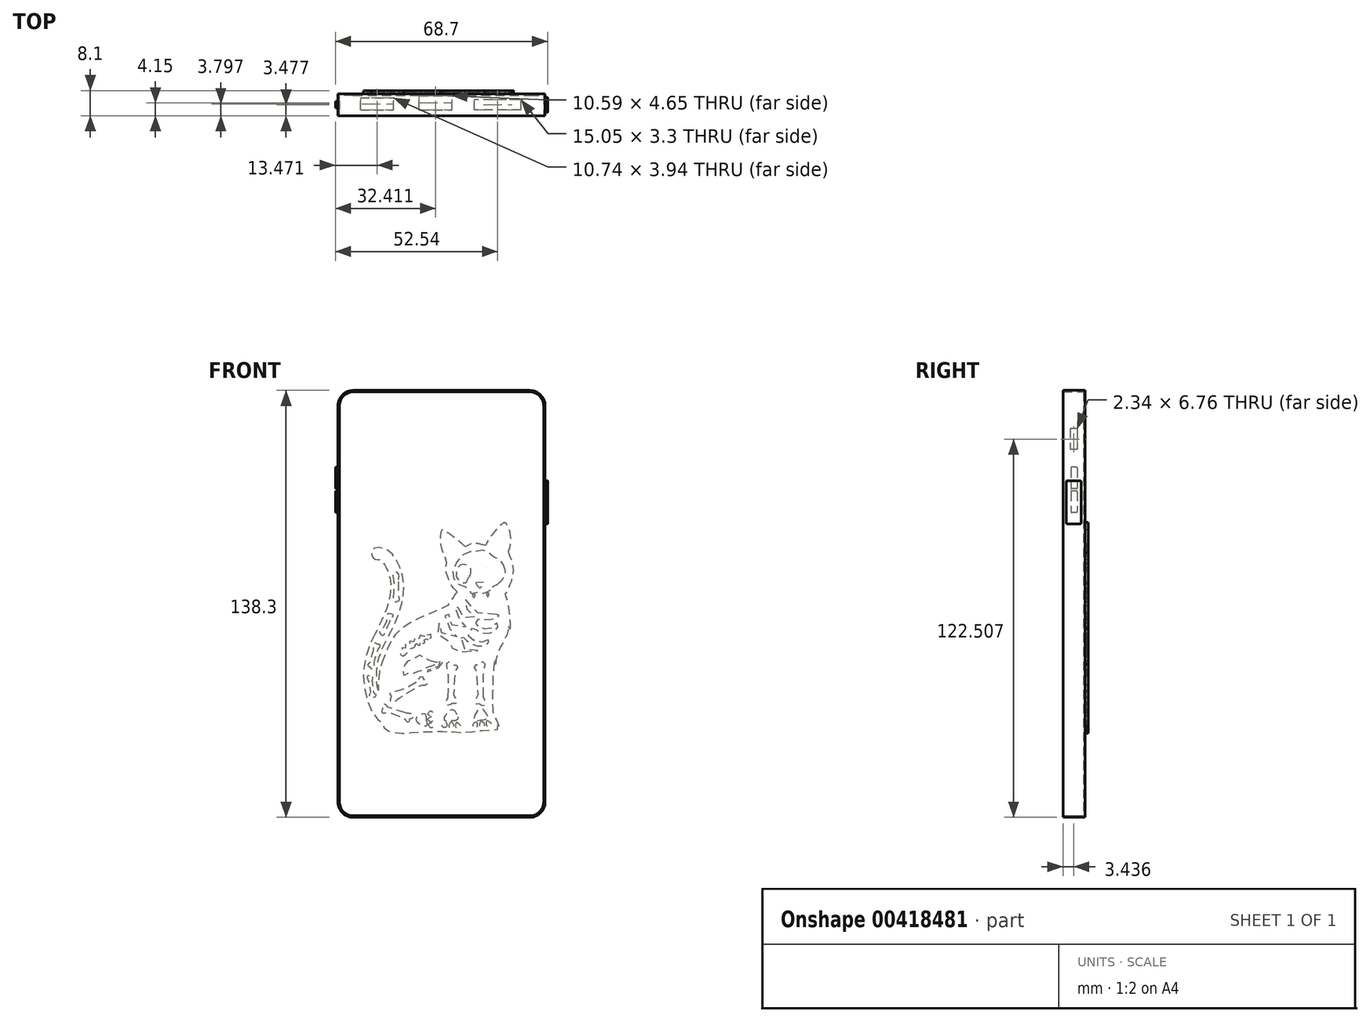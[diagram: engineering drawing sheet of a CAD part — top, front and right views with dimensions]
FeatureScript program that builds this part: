
annotation { "Feature Type Name" : "Feature", "Feature Type Description" : "" }
export const myFeature = defineFeature(function(context is Context, id is Id, definition is map)
    precondition{}
    {
        {
            var Q0;
            Q0=qCreatedBy(makeId("Front.planeOp"),FACE);
            var sketch = newSketch(context, id + "F0", { "sketchPlane" : qUnion([Q0])});
            skLineSegment(sketch, "E0", {"start": v(-28.9, 69.35) * mm, "end": v(28.2, 69.35) * mm});
            skLineSegment(sketch, "E1", {"start": v(-33.9, 64.35) * mm, "end": v(-33.9, -63.95) * mm});
            skLineSegment(sketch, "E2", {"start": v(-28.9, -68.95) * mm, "end": v(28.2, -68.95) * mm});
            skLineSegment(sketch, "E3", {"start": v(33.2, -63.95) * mm, "end": v(33.2, 64.35) * mm});
            skPoint(sketch, "E4.visualSharp", {"position": v(-33.9, 69.35) * mm});
            skArc(sketch, "E4.filletArc", {"start": v(-28.9, 69.35) * mm, "mid": v(-32.44, 67.89) * mm, "end": v(-33.9, 64.35) * mm});
            skPoint(sketch, "E5.visualSharp", {"position": v(33.2, 69.35) * mm});
            skArc(sketch, "E5.filletArc", {"start": v(33.2, 64.35) * mm, "mid": v(31.73, 67.89) * mm, "end": v(28.2, 69.35) * mm});
            skPoint(sketch, "E6.visualSharp", {"position": v(-33.9, -68.95) * mm});
            skArc(sketch, "E6.filletArc", {"start": v(-33.9, -63.95) * mm, "mid": v(-32.44, -67.48) * mm, "end": v(-28.9, -68.95) * mm});
            skPoint(sketch, "E7.visualSharp", {"position": v(33.2, -68.95) * mm});
            skArc(sketch, "E7.filletArc", {"start": v(28.2, -68.95) * mm, "mid": v(31.73, -67.48) * mm, "end": v(33.2, -63.95) * mm});
            skSolve(sketch);
        }
        {
            var Q0;
            Q0 = qSketchRegion(id + "F0", true);
            extrude(context, id + "F1", {"entities" : qUnion([Q0]), "oppositeDirection" : true, "depth" : 7.1 * mm});
        }
        {
            var Q0;
            Q0=makeQuery(id+"F1.opExtrude","CAP_FACE",FACE,{"disambiguationData":[OSD([sQuery(id+"F0.wireOp",EDGE,"E0"),sQuery(id+"F0.wireOp",EDGE,"E1"),sQuery(id+"F0.wireOp",EDGE,"E2"),sQuery(id+"F0.wireOp",EDGE,"E3"),sQuery(id+"F0.wireOp",EDGE,"E4.filletArc"),sQuery(id+"F0.wireOp",EDGE,"E5.filletArc"),sQuery(id+"F0.wireOp",EDGE,"E6.filletArc"),sQuery(id+"F0.wireOp",EDGE,"E7.filletArc")])],"isStart":true});
            shell(context, id + "F2", {"entities" : qUnion([Q0]), "thickness" : .5 * mm});
        }
        {
            var Q0;
            Q0=makeQuery(id+"F1.opExtrude","CAP_FACE",FACE,{"disambiguationData":[OSD([sQuery(id+"F0.wireOp",EDGE,"E0"),sQuery(id+"F0.wireOp",EDGE,"E1"),sQuery(id+"F0.wireOp",EDGE,"E2"),sQuery(id+"F0.wireOp",EDGE,"E3"),sQuery(id+"F0.wireOp",EDGE,"E4.filletArc"),sQuery(id+"F0.wireOp",EDGE,"E5.filletArc"),sQuery(id+"F0.wireOp",EDGE,"E6.filletArc"),sQuery(id+"F0.wireOp",EDGE,"E7.filletArc")])],"isStart":false});
            var sketch = newSketch(context, id + "F3", { "sketchPlane" : qUnion([Q0])});
            skFitSpline(sketch, "E8", {"points": [v(-13.75, 19.14) * mm, v(-10.8, 19.76) * mm, v(-9.24, 19.6) * mm, v(-7.3, 18.71) * mm], "startDerivative": vector(8.18, 2.1) * mm, "endDerivative": vector(6.13, -3.18) * mm});
            skFitSpline(sketch, "E9", {"points": [v(-7.3, 18.71) * mm, v(-2.53, 22.68) * mm, v(0.07, 24.22) * mm], "startDerivative": vector(8.63, 7.6) * mm, "endDerivative": vector(5.95, 3.13) * mm});
            skFitSpline(sketch, "E10", {"points": [v(0.07, 24.22) * mm, v(0.61, 23.11) * mm, v(0.48, 18.65) * mm, v(-0.34, 16.29) * mm, v(-1.06, 14.13) * mm, v(-1.11, 12.11) * mm], "startDerivative": vector(4.44, -5.76) * mm, "endDerivative": vector(0.6, -10.88) * mm});
            skPoint(sketch, "E11", {"position": v(-1, 14.49) * mm});
            skFitSpline(sketch, "E12", {"points": [v(-4.66, 4.1) * mm, v(-3.1, 5.86) * mm, v(-1.59, 9.13) * mm, v(-1.11, 10.96) * mm, v(-1.26, 13.19) * mm, v(-1.49, 13.68) * mm], "startDerivative": vector(7.4, 6.82) * mm, "endDerivative": vector(-2.36, 3.52) * mm});
            skPoint(sketch, "E13", {"position": v(-1.33, 13.4) * mm});
            skFitSpline(sketch, "E14", {"points": [v(-1.33, 13.4) * mm, v(-1, 14.49) * mm], "startDerivative": vector(0.34, 1.08) * mm, "endDerivative": vector(0.34, 1.08) * mm});
            skFitSpline(sketch, "E15", {"points": [v(-4.66, 4.1) * mm, v(-3.39, 2.35) * mm, v(-1.71, -0.16) * mm, v(-1.12, -0.54) * mm, v(1.45, -1.81) * mm, v(8.52, -4.89) * mm, v(13.7, -8.2) * mm, v(16.45, -11.42) * mm, v(18.96, -17.08) * mm], "startDerivative": vector(12.67, -15.98) * mm, "endDerivative": vector(14.8, -38.4) * mm});
            skFitSpline(sketch, "E16", {"points": [v(18.96, -17.08) * mm, v(19.63, -18.76) * mm, v(20.52, -22.45) * mm, v(20.8, -27.9) * mm], "startDerivative": vector(2.79, -6.33) * mm, "endDerivative": vector(0.11, -13.53) * mm});
            skFitSpline(sketch, "E17", {"points": [v(20.8, -27.9) * mm, v(21.2, -26.1) * mm, v(21.39, -22.24) * mm, v(21.1, -19.46) * mm, v(19.88, -15.17) * mm, v(16.94, -9.1) * mm, v(14.27, -3.24) * mm, v(12.78, 3.05) * mm, v(12.78, 8.38) * mm, v(14.64, 13.9) * mm, v(16.48, 16.52) * mm, v(17.97, 17.67) * mm, v(19.47, 18.3) * mm, v(21.06, 18.53) * mm, v(22.3, 18.09) * mm, v(22.98, 17.08) * mm, v(22.93, 15.74) * mm], "startDerivative": vector(9.4, 33.27) * mm, "endDerivative": vector(-5.81, -34.1) * mm});
            skFitSpline(sketch, "E18", {"points": [v(22.93, 15.74) * mm, v(22.33, 15.02) * mm, v(21.27, 14.56) * mm, v(20.64, 14.52) * mm, v(19.76, 14.06) * mm, v(18.86, 13) * mm, v(18.16, 11.68) * mm, v(17.2, 9.11) * mm, v(16.86, 7.25) * mm, v(16.84, 4.77) * mm, v(17.1, 2.73) * mm, v(18.22, -1.54) * mm, v(21.9, -9.52) * mm], "startDerivative": vector(-8.6, -13.84) * mm, "endDerivative": vector(24.76, -49.17) * mm});
            skFitSpline(sketch, "E19", {"points": [v(21.9, -9.52) * mm, v(23.63, -13.21) * mm, v(25.25, -18.74) * mm, v(25.63, -22.6) * mm, v(25.2, -28) * mm, v(23.21, -33.98) * mm, v(21.48, -36.73) * mm, v(19.95, -38.07) * mm, v(19.63, -38.31) * mm, v(19.34, -39.1) * mm, v(18.63, -40.18) * mm, v(17.77, -40.87) * mm, v(16.48, -41.33) * mm, v(14.4, -41.63) * mm, v(12.59, -41.75) * mm, v(8.94, -41.35) * mm, v(-0.57, -41.15) * mm, v(-4.1, -41.33) * mm, v(-6.93, -41.44) * mm, v(-11.75, -40.98) * mm, v(-14.02, -40.64) * mm, v(-17.24, -40.62) * mm, v(-17.7, -40.49) * mm, v(-17.9, -40.18) * mm, v(-17.84, -38.94) * mm], "startDerivative": vector(33.87, -64.85) * mm, "endDerivative": vector(6.36, 50.04) * mm});
            skFitSpline(sketch, "E20", {"points": [v(-17.84, -38.94) * mm, v(-18.18, -39.46) * mm], "startDerivative": vector(-0.34, -0.51) * mm, "endDerivative": vector(-0.34, -0.51) * mm});
            skFitSpline(sketch, "E21", {"points": [v(-18.18, -39.46) * mm, v(-18.25, -39.36) * mm, v(-17.53, -37.44) * mm, v(-16.78, -36.22) * mm, v(-16.5, -35.6) * mm, v(-16.41, -34.86) * mm, v(-16.2, -29.22) * mm, v(-16.34, -27.36) * mm, v(-16.4, -23.73) * mm, v(-16.5, -22.25) * mm, v(-16.92, -18.19) * mm], "startDerivative": vector(-3.64, 1.98) * mm, "endDerivative": vector(-3.4, 31.6) * mm});
            skFitSpline(sketch, "E22", {"points": [v(-16.92, -18.19) * mm, v(-17.05, -18.6) * mm, v(-17.11, -19.12) * mm, v(-17.25, -19.38) * mm], "startDerivative": vector(-0.43, -1.1) * mm, "endDerivative": vector(-0.56, -0.8) * mm});
            skFitSpline(sketch, "E23", {"points": [v(-17.25, -19.38) * mm, v(-17.3, -19.17) * mm, v(-17.34, -18.44) * mm, v(-17.44, -17.73) * mm, v(-17.7, -16.6) * mm, v(-19.08, -13.32) * mm, v(-20.52, -10.52) * mm, v(-21.15, -9.13) * mm, v(-21.37, -7.91) * mm, v(-21.38, -7.08) * mm], "startDerivative": vector(-1.24, 3.7) * mm, "endDerivative": vector(0.13, 8.82) * mm});
            skFitSpline(sketch, "E24", {"points": [v(-21.38, -7.08) * mm, v(-21.61, -7.68) * mm, v(-21.94, -7.86) * mm], "startDerivative": vector(-0.3, -1.25) * mm, "endDerivative": vector(-0.83, -0.27) * mm});
            skFitSpline(sketch, "E25", {"points": [v(-21.94, -7.86) * mm, v(-21.94, -7.06) * mm, v(-21.82, -4.78) * mm, v(-21.57, -2.25) * mm, v(-21.29, -0.3) * mm, v(-20.63, 2.35) * mm, v(-20.28, 3.23) * mm, v(-20.44, 3.55) * mm, v(-21.26, 4.87) * mm, v(-21.56, 5.86) * mm, v(-22.06, 7.03) * mm, v(-22.72, 9.14) * mm, v(-22.92, 11.02) * mm, v(-22.8, 12.55) * mm, v(-22.25, 14.64) * mm, v(-21.41, 16.74) * mm], "startDerivative": vector(-0.23, 14.82) * mm, "endDerivative": vector(11.2, 26.26) * mm});
            skFitSpline(sketch, "E26", {"points": [v(-21.41, 16.74) * mm, v(-21.33, 17) * mm, v(-21.55, 17.65) * mm, v(-21.82, 18.76) * mm, v(-21.98, 20.09) * mm, v(-22.05, 21.6) * mm, v(-21.82, 23.67) * mm, v(-21.16, 25.22) * mm, v(-20.62, 26.1) * mm, v(-20.17, 26.49) * mm, v(-19.79, 26.52) * mm, v(-19.05, 25.9) * mm, v(-17.69, 24.62) * mm, v(-15.96, 22.5) * mm, v(-15.06, 21.28) * mm, v(-14.3, 19.98) * mm, v(-13.98, 19.26) * mm, v(-13.75, 19.14) * mm], "startDerivative": vector(4.25, 8) * mm, "endDerivative": vector(8.55, -2.19) * mm});
            skLineSegment(sketch, "E27", {"start": v(-13.17, 7.17) * mm, "end": v(-10.84, 7.07) * mm});
            skFitSpline(sketch, "E28", {"points": [v(-10.84, 7.07) * mm, v(-10.8, 6.94) * mm, v(-11.28, 6.07) * mm, v(-11.99, 5.42) * mm, v(-12.22, 5.43) * mm, v(-13.03, 6.77) * mm, v(-13.17, 7.17) * mm], "startDerivative": vector(0.97, -1.26) * mm, "endDerivative": vector(-0.6, 2.16) * mm});
            skFitSpline(sketch, "E29", {"points": [v(-17.75, 6.52) * mm, v(-18.1, 6.9) * mm, v(-18.72, 7.4) * mm, v(-19.25, 7.94) * mm, v(-19.81, 8.86) * mm, v(-20.17, 9.66) * mm, v(-20.31, 10.5) * mm, v(-20.23, 11.38) * mm, v(-19.91, 12.18) * mm], "startDerivative": vector(-3.1, 3.7) * mm, "endDerivative": vector(2.86, 6.13) * mm});
            skFitSpline(sketch, "E30", {"points": [v(-20.23, 11.38) * mm, v(-20, 12.13) * mm, v(-19.8, 12.46) * mm, v(-19.76, 12.7) * mm, v(-19.59, 13.12) * mm, v(-19.39, 13.53) * mm, v(-19, 14.07) * mm, v(-18.4, 14.68) * mm, v(-17.58, 15.03) * mm, v(-16.68, 15.34) * mm, v(-15.86, 15.92) * mm, v(-15.3, 16.46) * mm, v(-14.54, 17) * mm, v(-13.58, 17.36) * mm, v(-13.26, 17.52) * mm, v(-12.36, 17.55) * mm, v(-11.58, 17.4) * mm, v(-10.71, 17.1) * mm, v(-9.96, 17.02) * mm, v(-9.26, 17.09) * mm, v(-8.56, 17) * mm, v(-7.4, 16.57) * mm, v(-6.36, 15.88) * mm, v(-5.23, 14.71) * mm, v(-4.18, 13.12) * mm, v(-3.44, 11.52) * mm, v(-3.27, 9.92) * mm, v(-3.39, 8.92) * mm, v(-3.99, 7.68) * mm, v(-4.62, 6.91) * mm, v(-5.56, 6.37) * mm, v(-6.15, 6.07) * mm, v(-7.2, 5.78) * mm, v(-7.93, 5.6) * mm, v(-8.3, 5.5) * mm, v(-8.57, 5.28) * mm, v(-8.63, 4.89) * mm, v(-8.64, 4.26) * mm, v(-8.78, 3.84) * mm, v(-9.08, 3.64) * mm, v(-9.6, 3.8) * mm, v(-10.07, 4.01) * mm, v(-10.6, 4) * mm, v(-11.1, 3.59) * mm, v(-11.26, 3.52) * mm, v(-11.5, 3.69) * mm, v(-11.8, 4.07) * mm, v(-12, 4.16) * mm, v(-12.39, 4.11) * mm, v(-12.68, 3.83) * mm, v(-13.01, 3.64) * mm, v(-13.4, 3.8) * mm, v(-13.88, 4.16) * mm, v(-14.23, 4.2) * mm, v(-14.48, 4.16) * mm, v(-14.66, 4.05) * mm, v(-14.85, 4.13) * mm, v(-15.14, 4.46) * mm, v(-15.23, 4.59) * mm, v(-15.43, 4.58) * mm, v(-15.82, 4.37) * mm, v(-16.01, 4.26) * mm, v(-16.23, 4.38) * mm, v(-16.29, 4.71) * mm, v(-16.36, 4.89) * mm, v(-16.3, 5.08) * mm, v(-16.27, 5.58) * mm, v(-16.3, 5.87) * mm, v(-16.49, 6.1) * mm, v(-17.36, 6.24) * mm, v(-17.6, 6.28) * mm, v(-17.75, 6.52) * mm], "startDerivative": vector(10.89, 50.55) * mm, "endDerivative": vector(-14.38, 29.48) * mm});
            skFitSpline(sketch, "E31", {"points": [v(-14.6, 2.43) * mm, v(-14.76, 2.72) * mm, v(-14.9, 3.05) * mm, v(-14.97, 3.5) * mm, v(-14.89, 3.66) * mm, v(-14.7, 3.75) * mm, v(-14.56, 3.64) * mm, v(-14.3, 3.55) * mm, v(-14.24, 3.4) * mm, v(-14.38, 2.95) * mm, v(-14.6, 2.43) * mm]});
            skFitSpline(sketch, "E32", {"points": [v(-10.23, 2.12) * mm, v(-10.05, 2.34) * mm, v(-9.77, 2.78) * mm, v(-9.7, 3.1) * mm, v(-9.74, 3.32) * mm, v(-9.93, 3.42) * mm, v(-10.33, 3.37) * mm, v(-10.42, 3.3) * mm, v(-10.4, 3.08) * mm, v(-10.29, 2.35) * mm, v(-10.23, 2.12) * mm]});
            skFitSpline(sketch, "E33", {"points": [v(-15.78, 8.5) * mm, v(-15.71, 8.74) * mm, v(-15.46, 9.05) * mm, v(-14.87, 9.68) * mm, v(-14.47, 10.43) * mm, v(-14.34, 10.93) * mm, v(-14.3, 11.47) * mm, v(-14.23, 12) * mm, v(-14.41, 12.18) * mm], "startDerivative": vector(0.41, 2.77) * mm, "endDerivative": vector(-2.6, 1.59) * mm});
            skFitSpline(sketch, "E34", {"points": [v(-14.23, 12) * mm, v(-14.42, 12.34) * mm, v(-14.89, 12.92) * mm, v(-15.93, 13.54) * mm, v(-17.03, 13.68) * mm, v(-17.6, 13.49) * mm, v(-18.06, 13.07) * mm, v(-18.51, 12.53) * mm, v(-18.9, 11.8) * mm, v(-19.07, 11.31) * mm, v(-19.15, 10.9) * mm, v(-19.2, 10.23) * mm, v(-18.71, 9.04) * mm, v(-18.14, 8.3) * mm, v(-17.4, 7.86) * mm, v(-16.5, 7.79) * mm, v(-15.91, 8.1) * mm, v(-15.8, 8.32) * mm, v(-15.8, 8.44) * mm, v(-15.78, 8.5) * mm], "startDerivative": vector(-3.88, 7.93) * mm, "endDerivative": vector(2.17, 2.92) * mm});
            skFitSpline(sketch, "E35", {"points": [v(-8.67, 8.9) * mm, v(-9, 9.6) * mm, v(-9.16, 10.18) * mm, v(-9.17, 10.9) * mm, v(-9.13, 11.46) * mm, v(-8.31, 12.4) * mm, v(-7.48, 12.78) * mm, v(-6.84, 12.94) * mm, v(-5.7, 12.8) * mm, v(-4.8, 11.69) * mm, v(-4.45, 10.73) * mm, v(-4.43, 9.57) * mm, v(-4.34, 9.4) * mm, v(-4.5, 8.9) * mm, v(-5.08, 8.04) * mm, v(-5.62, 7.45) * mm, v(-6.7, 7.08) * mm, v(-7.57, 7.15) * mm, v(-7.98, 7.48) * mm, v(-8, 7.94) * mm, v(-8.16, 8.35) * mm, v(-8.67, 8.9) * mm]});
            skFitSpline(sketch, "E36", {"points": [v(2.3, -18.78) * mm, v(2.89, -19.07) * mm, v(3.33, -19.26) * mm, v(3.79, -19.1) * mm, v(4.24, -18.37) * mm, v(4.8, -17.5) * mm, v(5.75, -16.78) * mm, v(6.91, -16.4) * mm, v(7.89, -16.46) * mm, v(8.86, -16.76) * mm, v(9.83, -17.41) * mm, v(10.1, -17.9) * mm, v(10.4, -18.23) * mm, v(10.58, -18.6) * mm, v(10.96, -18.98) * mm, v(11, -18.77) * mm, v(11.1, -18.56) * mm, v(11.28, -18.37) * mm, v(11.45, -18.27) * mm, v(11.75, -18.3) * mm, v(12, -18.45) * mm, v(12.25, -18.78) * mm, v(12.36, -19.3) * mm, v(12.2, -19.86) * mm, v(12.15, -19.97) * mm, v(12.25, -20.2) * mm, v(12.41, -20.4) * mm, v(12.62, -20.75) * mm, v(12.77, -21.04) * mm, v(12.9, -21.5) * mm, v(13.03, -22.03) * mm, v(13.13, -22.28) * mm, v(13.1, -22.56) * mm, v(12.82, -22.77) * mm, v(12.6, -22.8) * mm, v(12.58, -22.97) * mm, v(12.53, -23.04) * mm, v(12.46, -23.03) * mm, v(12.45, -22.84) * mm, v(12.42, -22.79) * mm, v(12.28, -22.82) * mm, v(12.21, -22.81) * mm, v(12.18, -22.76) * mm, v(12.12, -22.76) * mm, v(12.06, -22.8) * mm, v(11.97, -22.78) * mm, v(11.95, -22.7) * mm, v(11.94, -22.57) * mm, v(11.74, -22.56) * mm, v(11.4, -22.56) * mm, v(11.22, -22.48) * mm, v(11.01, -22.43) * mm, v(10.82, -22.22) * mm, v(10.6, -22) * mm, v(10.4, -21.86) * mm, v(10.17, -21.9) * mm, v(10.05, -21.84) * mm, v(10, -21.86) * mm, v(10.05, -21.98) * mm, v(10.1, -22.03) * mm, v(10.06, -22.1) * mm, v(10, -22.15) * mm, v(10.04, -22.22) * mm, v(10.04, -22.3) * mm, v(9.96, -22.33) * mm, v(9.89, -22.3) * mm, v(9.65, -22.13) * mm, v(9.58, -22.12) * mm, v(9.59, -22.2) * mm, v(9.7, -22.35) * mm, v(9.66, -22.4) * mm, v(9.53, -22.44) * mm, v(9.45, -22.36) * mm, v(9.19, -22.05) * mm, v(8.95, -21.83) * mm, v(8.51, -21.7) * mm, v(8.28, -21.68) * mm, v(7.8, -21.37) * mm, v(7.75, -21.44) * mm, v(7.68, -21.52) * mm, v(7.56, -21.51) * mm, v(7.5, -21.6) * mm, v(7.56, -21.68) * mm, v(7.54, -21.77) * mm, v(7.44, -21.8) * mm, v(7.28, -21.64) * mm, v(7.19, -21.49) * mm, v(7.08, -21.43) * mm, v(7.03, -21.35) * mm, v(6.96, -21.34) * mm, v(6.96, -21.74) * mm, v(6.91, -21.74) * mm, v(6.88, -21.82) * mm, v(6.8, -21.86) * mm, v(6.72, -21.82) * mm, v(6.73, -21.58) * mm, v(6.73, -21.44) * mm, v(6.5, -21.23) * mm, v(6.15, -21) * mm, v(5.88, -20.82) * mm, v(5.3, -20.66) * mm, v(5, -20.58) * mm, v(4.83, -20.41) * mm, v(4.8, -20.32) * mm, v(4.83, -20.24) * mm, v(4.9, -20.19) * mm, v(4.85, -20.13) * mm, v(4.7, -20.05) * mm, v(4.38, -19.88) * mm, v(3.88, -19.71) * mm, v(3.27, -19.7) * mm, v(2.8, -19.52) * mm, v(2.34, -19.23) * mm, v(1.8, -18.9) * mm, v(1.43, -18.72) * mm, v(1.17, -18.55) * mm, v(0.74, -18.53) * mm, v(0.49, -18.63) * mm, v(0.32, -18.94) * mm, v(0.34, -19.35) * mm, v(0.9, -19.78) * mm, v(2.16, -20.42) * mm, v(3.45, -20.86) * mm, v(4.38, -21.13) * mm, v(5.08, -21.43) * mm, v(5.63, -22) * mm, v(5.72, -22.22) * mm, v(5.58, -22.3) * mm, v(5.35, -22.2) * mm, v(5.07, -21.88) * mm, v(4.83, -21.65) * mm, v(3.96, -21.35) * mm, v(2.31, -20.86) * mm, v(1.15, -20.3) * mm, v(1, -20.2) * mm, v(0.6, -19.97) * mm, v(0.08, -19.5) * mm, v(-0.05, -19.06) * mm, v(0.06, -18.66) * mm, v(0.3, -18.32) * mm, v(0.72, -18.2) * mm, v(1.3, -18.26) * mm, v(2.3, -18.78) * mm]});
            skFitSpline(sketch, "E37", {"points": [v(14.38, 7.46) * mm, v(14.38, 3.34) * mm, v(14.25, 2.46) * mm, v(14.1, 1.68) * mm, v(14.2, 1.18) * mm, v(14.57, 0.91) * mm, v(14.78, 0.95) * mm, v(14.97, 0.76) * mm, v(15.43, 0.69) * mm, v(15.83, 1.09) * mm, v(15.98, 1.68) * mm, v(15.85, 2.67) * mm, v(15.74, 4.6) * mm, v(15.72, 7.42) * mm, v(15.83, 7.9) * mm, v(15.83, 8.58) * mm, v(15.98, 9.48) * mm, v(16.02, 10.2) * mm, v(15.77, 10.6) * mm, v(15.37, 10.68) * mm, v(14.7, 10.3) * mm, v(14.23, 9.73) * mm, v(14.21, 9.06) * mm, v(14.34, 8.54) * mm, v(14.38, 7.46) * mm]});
            skFitSpline(sketch, "E38", {"points": [v(17.04, -5.14) * mm, v(17.66, -6.66) * mm, v(18.5, -8.28) * mm, v(18.95, -9.04) * mm, v(18.95, -9.69) * mm, v(19.09, -10.08) * mm, v(19.53, -10.22) * mm, v(19.86, -9.97) * mm, v(19.98, -9.53) * mm, v(20.23, -9.19) * mm, v(20.35, -8.84) * mm, v(20.16, -8.45) * mm, v(19.6, -8.05) * mm, v(19.18, -7.53) * mm, v(17.97, -4.9) * mm, v(17.94, -3.82) * mm, v(17.76, -3.11) * mm, v(17.5, -2.8) * mm, v(17.19, -2.81) * mm, v(16.9, -3) * mm, v(16.43, -3.08) * mm, v(16.17, -3.3) * mm, v(16.15, -3.78) * mm, v(16.47, -4.22) * mm, v(17.04, -5.14) * mm]});
            skFitSpline(sketch, "E39", {"points": [v(22.95, -16.77) * mm, v(22.45, -15.1) * mm, v(22.4, -14.22) * mm, v(22.5, -13.33) * mm, v(22.35, -12.85) * mm, v(22.06, -12.47) * mm, v(21.67, -12.43) * mm, v(21.39, -12.72) * mm, v(21.27, -12.82) * mm, v(20.84, -12.8) * mm, v(20.5, -13.05) * mm], "startDerivative": vector(-3.52, 10.42) * mm, "endDerivative": vector(-3.57, -3.84) * mm});
            skFitSpline(sketch, "E40", {"points": [v(20.84, -12.8) * mm, v(20.68, -12.8) * mm, v(20.4, -13) * mm, v(20.38, -13.45) * mm, v(20.67, -14.1) * mm, v(21.02, -14.7) * mm, v(21.39, -15.7) * mm, v(22.16, -18.23) * mm, v(22.24, -19.24) * mm, v(22.24, -20.24) * mm, v(22.24, -20.59) * mm, v(22.65, -20.9) * mm, v(23.05, -20.78) * mm, v(23.33, -20.5) * mm, v(23.78, -20.23) * mm, v(24.06, -19.93) * mm, v(24.06, -19.42) * mm, v(23.63, -18.93) * mm, v(23.4, -18.53) * mm, v(23.27, -17.78) * mm, v(22.95, -16.77) * mm], "startDerivative": vector(-5.9, 0.94) * mm, "endDerivative": vector(-5.98, 15.91) * mm});
            skFitSpline(sketch, "E41", {"points": [v(23.63, -23.22) * mm, v(23.9, -23.05) * mm, v(24.32, -23.1) * mm, v(24.54, -23.55) * mm, v(24.26, -24.32) * mm, v(23.98, -24.93) * mm, v(23.38, -28.4) * mm, v(23.42, -28.72) * mm, v(23.64, -28.96) * mm, v(23.72, -29.46) * mm, v(23.72, -29.88) * mm, v(23.4, -30.2) * mm, v(23.05, -30.16) * mm, v(22.84, -29.9) * mm, v(22.5, -29.9) * mm, v(22.09, -30.05) * mm, v(21.65, -29.74) * mm, v(21.53, -29.45) * mm, v(21.61, -29.14) * mm, v(21.95, -28.95) * mm, v(22.21, -28.74) * mm, v(22.3, -28.28) * mm, v(22.72, -24.87) * mm, v(22.68, -24.38) * mm, v(22.58, -23.86) * mm, v(22.61, -23.46) * mm, v(22.83, -23.13) * mm, v(23.18, -23.03) * mm, v(23.63, -23.22) * mm]});
            skFitSpline(sketch, "E42", {"points": [v(4.28, -35.9) * mm, v(4.69, -35.7) * mm, v(4.76, -35.38) * mm, v(4.42, -34.86) * mm, v(3.96, -34.48) * mm, v(3.5, -34.55) * mm, v(3.21, -35.04) * mm, v(3.28, -35.7) * mm, v(3.85, -36.02) * mm, v(4.28, -35.9) * mm]});
            skFitSpline(sketch, "E43", {"points": [v(4.05, -36.5) * mm, v(4.65, -36.94) * mm, v(4.8, -37.18) * mm, v(4.77, -37.4) * mm, v(4.54, -37.6) * mm, v(4.06, -37.88) * mm, v(3.62, -37.93) * mm, v(3.33, -37.78) * mm, v(3.13, -37.57) * mm, v(3.08, -36.98) * mm, v(3.31, -36.55) * mm, v(3.6, -36.33) * mm, v(4.05, -36.5) * mm]});
            skFitSpline(sketch, "E44", {"points": [v(3.85, -38.4) * mm, v(4.27, -38.46) * mm, v(4.55, -38.82) * mm, v(4.52, -39.25) * mm, v(3.9, -39.8) * mm, v(3.39, -39.8) * mm, v(3, -39.46) * mm, v(2.93, -38.97) * mm, v(3.23, -38.53) * mm, v(3.85, -38.4) * mm]});
            skFitSpline(sketch, "E45", {"points": [v(5.17, -37.08) * mm, v(5.23, -36.45) * mm, v(5.4, -35.82) * mm, v(5.92, -35.36) * mm, v(6.57, -35.47) * mm, v(7.48, -35.95) * mm, v(7.9, -36.26) * mm, v(8.37, -36.47) * mm, v(8.64, -36.87) * mm, v(8.5, -37.7) * mm, v(7.99, -38.24) * mm, v(7.35, -38.67) * mm, v(6.8, -38.97) * mm, v(6.27, -39.24) * mm, v(5.9, -39.32) * mm, v(5.4, -39.3) * mm, v(5.02, -38.9) * mm, v(4.97, -38.46) * mm, v(5.12, -37.82) * mm, v(5.2, -37.47) * mm, v(5.17, -37.08) * mm]});
            skFitSpline(sketch, "E46", {"points": [v(-1.4, -38.56) * mm, v(-1.4, -39.2) * mm, v(-1.07, -39.74) * mm, v(-0.46, -39.86) * mm, v(0.1, -39.46) * mm, v(0.13, -38.94) * mm, v(-0.23, -38.49) * mm, v(-0.72, -38.14) * mm, v(-1.15, -38.2) * mm, v(-1.4, -38.56) * mm]});
            skFitSpline(sketch, "E47", {"points": [v(-3.45, -38.69) * mm, v(-3.13, -38.28) * mm, v(-2.92, -38.08) * mm, v(-2.62, -38.1) * mm, v(-2.37, -38.42) * mm, v(-2.1, -38.89) * mm, v(-2.02, -39.35) * mm, v(-2.17, -39.68) * mm, v(-2.6, -39.87) * mm, v(-3.33, -39.72) * mm, v(-3.61, -39.5) * mm, v(-3.72, -39.23) * mm, v(-3.45, -38.69) * mm]});
            skFitSpline(sketch, "E48", {"points": [v(-5.45, -38.77) * mm, v(-5.17, -38.54) * mm, v(-4.88, -38.28) * mm, v(-4.6, -38.24) * mm, v(-4.34, -38.5) * mm, v(-4.12, -39.04) * mm, v(-4.2, -39.7) * mm, v(-4.48, -39.9) * mm, v(-5.16, -39.94) * mm, v(-5.52, -39.8) * mm, v(-5.76, -39.5) * mm, v(-5.78, -39.14) * mm, v(-5.45, -38.77) * mm]});
            skFitSpline(sketch, "E49", {"points": [v(-4.9, -36.4) * mm, v(-5, -36.76) * mm, v(-4.81, -37.25) * mm, v(-4.07, -37.67) * mm, v(-3.11, -37.67) * mm, v(-2.43, -37.6) * mm, v(-1.72, -37.78) * mm, v(-0.95, -37.7) * mm, v(-0.59, -37.32) * mm, v(-0.63, -36.65) * mm, v(-0.67, -36.43) * mm, v(-0.93, -36) * mm, v(-1.34, -35.4) * mm, v(-1.83, -34.74) * mm, v(-2.58, -34.19) * mm, v(-3.2, -34.02) * mm, v(-3.77, -34.18) * mm, v(-4.08, -34.62) * mm, v(-4.35, -35.3) * mm, v(-4.8, -36.04) * mm, v(-4.9, -36.4) * mm]});
            skFitSpline(sketch, "E50", {"points": [v(11.99, -35.12) * mm, v(17.44, -33.38) * mm, v(17.85, -33.13) * mm, v(18.16, -32.7) * mm, v(18.51, -32.33) * mm, v(19.13, -32.34) * mm, v(19.58, -32.7) * mm, v(19.54, -33.42) * mm, v(19.4, -33.7) * mm, v(19.49, -33.98) * mm, v(19.74, -34.48) * mm, v(19.57, -34.97) * mm, v(19.12, -35.15) * mm, v(18.35, -35.04) * mm, v(17.9, -34.87) * mm, v(17.45, -34.93) * mm, v(12.62, -36.86) * mm, v(11.88, -37.6) * mm, v(11.62, -37.93) * mm, v(11.15, -37.93) * mm], "startDerivative": vector(50.03, 15.27) * mm, "endDerivative": vector(-13.04, 2.19) * mm});
            skFitSpline(sketch, "E51", {"points": [v(11.62, -37.93) * mm, v(11.41, -38.05) * mm, v(11.03, -38) * mm, v(10.74, -37.72) * mm, v(10.65, -37.33) * mm, v(10.67, -37.03) * mm, v(10.39, -36.94) * mm, v(10.12, -36.89) * mm, v(9.72, -36.7) * mm, v(9.5, -36.18) * mm, v(9.53, -35.76) * mm, v(9.92, -35.4) * mm, v(10.56, -35.33) * mm, v(11.13, -35.26) * mm, v(11.99, -35.12) * mm], "startDerivative": vector(-3.5, -2.7) * mm, "endDerivative": vector(9.04, 1.48) * mm});
            skFitSpline(sketch, "E52", {"points": [v(8.53, -25.2) * mm, v(14.7, -28.16) * mm, v(15.9, -28.3) * mm, v(16.45, -28.2) * mm, v(16.95, -28.59) * mm, v(17.08, -29.22) * mm, v(16.72, -29.54) * mm, v(16.56, -29.75) * mm, v(16.77, -30.15) * mm, v(17.04, -30.74) * mm, v(16.88, -31.36) * mm, v(16.34, -31.67) * mm, v(15.45, -31.5) * mm, v(15.16, -31.04) * mm, v(14.66, -30.79) * mm, v(14.34, -30.47) * mm, v(7.26, -26.25) * mm, v(6.85, -26.12) * mm, v(6.1, -26.25) * mm, v(5.15, -25.91) * mm, v(4.81, -25.28) * mm, v(5.04, -24.73) * mm, v(5.95, -24.44) * mm, v(6.13, -24.07) * mm, v(6.38, -23.55) * mm, v(6.95, -23.37) * mm, v(7.58, -23.67) * mm, v(7.99, -24.37) * mm, v(8.53, -25.2) * mm]});
            skFitSpline(sketch, "E53", {"points": [v(-15.34, -38.16) * mm, v(-14.84, -37.8) * mm, v(-14.4, -37.68) * mm, v(-14.15, -37.93) * mm, v(-14.04, -38.57) * mm, v(-14.23, -39.19) * mm, v(-14.78, -39.32) * mm, v(-15.38, -39.2) * mm, v(-15.68, -38.82) * mm, v(-15.7, -38.5) * mm, v(-15.34, -38.16) * mm]});
            skFitSpline(sketch, "E54", {"points": [v(-13.44, -38.48) * mm, v(-12.8, -37.83) * mm, v(-12.57, -37.76) * mm, v(-12.35, -37.84) * mm, v(-12.07, -38.35) * mm, v(-11.9, -38.7) * mm, v(-11.95, -39.22) * mm, v(-12.17, -39.47) * mm, v(-12.59, -39.6) * mm, v(-13.27, -39.38) * mm, v(-13.54, -39.16) * mm, v(-13.63, -38.92) * mm, v(-13.57, -38.64) * mm, v(-13.44, -38.48) * mm]});
            skFitSpline(sketch, "E55", {"points": [v(-11.33, -39.07) * mm, v(-11.32, -38.63) * mm, v(-11, -38.22) * mm, v(-10.61, -38.14) * mm, v(-10.08, -38.54) * mm, v(-9.76, -39.1) * mm, v(-9.97, -39.68) * mm, v(-10.35, -39.9) * mm, v(-10.9, -39.86) * mm, v(-11.28, -39.52) * mm, v(-11.33, -39.07) * mm]});
            skFitSpline(sketch, "E56", {"points": [v(-14.55, -36.28) * mm, v(-14.58, -36.08) * mm, v(-14.17, -35.38) * mm, v(-13.62, -34.63) * mm, v(-13.13, -34.02) * mm, v(-12.83, -33.77) * mm, v(-12.24, -33.76) * mm, v(-11.77, -33.96) * mm, v(-11.22, -34.49) * mm, v(-10.68, -35.44) * mm, v(-10.28, -36.3) * mm, v(-10.19, -37.13) * mm, v(-10.4, -37.54) * mm, v(-10.89, -37.74) * mm, v(-11.54, -37.54) * mm, v(-12.16, -37.38) * mm, v(-13.08, -37.36) * mm, v(-13.67, -37.22) * mm, v(-14.32, -36.86) * mm, v(-14.55, -36.28) * mm]});
            skFitSpline(sketch, "E57", {"points": [v(-13.22, -29.86) * mm, v(-13.23, -22.21) * mm, v(-13.44, -21.43) * mm, v(-13.54, -20.75) * mm, v(-13.57, -20.27) * mm, v(-13.78, -19.66) * mm, v(-13.67, -18.99) * mm, v(-13.04, -18.56) * mm, v(-12.46, -18.59) * mm, v(-11.95, -19.07) * mm, v(-11.52, -19.68) * mm, v(-11.13, -19.52) * mm, v(-10.6, -19.6) * mm, v(-10.25, -19.98) * mm, v(-10.17, -20.63) * mm, v(-10.67, -21.28) * mm, v(-10.99, -22.57) * mm, v(-11.37, -29.05) * mm, v(-11.3, -29.6) * mm, v(-10.76, -30.47) * mm, v(-10.43, -31.23) * mm, v(-10.57, -31.9) * mm, v(-11.05, -32.22) * mm, v(-11.64, -32.13) * mm, v(-11.9, -32.08) * mm, v(-12.24, -32.32) * mm, v(-12.78, -32.67) * mm, v(-13.34, -32.73) * mm, v(-13.75, -32.43) * mm, v(-13.99, -31.9) * mm, v(-13.75, -30.99) * mm, v(-13.25, -30.47) * mm, v(-13.22, -29.86) * mm]});
            skFitSpline(sketch, "E58", {"points": [v(-1.77, -30.13) * mm, v(-1.78, -22.29) * mm, v(-1.54, -21.14) * mm, v(-1.52, -20.34) * mm, v(-1.29, -19.67) * mm, v(-1.54, -18.82) * mm, v(-2.19, -18.51) * mm, v(-2.87, -18.74) * mm, v(-3.27, -19.52) * mm, v(-3.6, -19.7) * mm, v(-3.86, -19.5) * mm, v(-4.3, -19.47) * mm, v(-4.74, -19.9) * mm, v(-4.9, -20.29) * mm, v(-4.72, -20.6) * mm, v(-4.34, -21.2) * mm, v(-4, -22.14) * mm, v(-3.6, -29) * mm, v(-3.63, -29.48) * mm, v(-4.05, -30.13) * mm, v(-4.44, -30.93) * mm, v(-4.5, -31.46) * mm, v(-4.17, -32.1) * mm, v(-3.35, -32.13) * mm, v(-3.06, -32.03) * mm, v(-2.8, -32.26) * mm, v(-2.15, -32.66) * mm, v(-1.46, -32.68) * mm, v(-1.14, -32.2) * mm, v(-1.08, -31.56) * mm, v(-1.42, -30.8) * mm, v(-1.73, -30.47) * mm, v(-1.77, -30.13) * mm]});
            skFitSpline(sketch, "E59", {"points": [v(4.14, -11.12) * mm, v(4.28, -10.8) * mm, v(4.18, -10.58) * mm, v(3.8, -10.58) * mm, v(3.5, -10.47) * mm, v(3.57, -10.26) * mm, v(3.74, -10.03) * mm, v(3.82, -9.52) * mm, v(4.05, -9.36) * mm, v(4.32, -9.69) * mm, v(4.7, -10) * mm, v(5.1, -9.76) * mm, v(5.33, -9.38) * mm, v(5.67, -9.44) * mm, v(5.92, -9.65) * mm, v(5.86, -9.89) * mm, v(5.78, -10.29) * mm, v(6.48, -10.61) * mm, v(6.91, -9.97) * mm, v(7.62, -10.16) * mm, v(7.41, -10.82) * mm, v(7.98, -11.25) * mm, v(8.46, -10.8) * mm, v(8.67, -10.7) * mm, v(9.18, -11.01) * mm, v(8.95, -11.5) * mm, v(9.65, -12.22) * mm, v(10.05, -12) * mm, v(10.3, -11.8) * mm, v(10.8, -12.15) * mm, v(10.57, -12.62) * mm, v(10.76, -13.14) * mm, v(11.12, -13.27) * mm, v(11.62, -12.76) * mm, v(12.16, -13.23) * mm, v(11.99, -13.4) * mm, v(11.78, -13.75) * mm, v(12.35, -14.32) * mm, v(12.63, -14.2) * mm, v(12.89, -13.96) * mm, v(13.37, -14.34) * mm, v(13.08, -14.76) * mm, v(12.95, -15.1) * mm, v(13.81, -15.74) * mm, v(13.95, -15.96) * mm, v(13.78, -16.11) * mm, v(13.49, -16.22) * mm, v(13.23, -16.64) * mm, v(12.95, -16.77) * mm, v(12.6, -16.3) * mm, v(12.4, -15.93) * mm, v(11.99, -15.96) * mm, v(11.74, -16.3) * mm, v(11.21, -16) * mm, v(11.5, -15.5) * mm, v(11.37, -15.16) * mm, v(10.97, -14.9) * mm, v(10.62, -15.29) * mm, v(9.89, -14.9) * mm, v(10.25, -14.34) * mm, v(10.16, -14) * mm, v(9.78, -13.7) * mm, v(9.28, -13.9) * mm, v(9.08, -14.06) * mm, v(8.6, -13.74) * mm, v(8.95, -13.22) * mm], "startDerivative": vector(14.36, 24.4) * mm, "endDerivative": vector(34.16, 29.59) * mm});
            skFitSpline(sketch, "E60", {"points": [v(8.75, -13.4) * mm, v(8.88, -13.1) * mm, v(8.55, -12.71) * mm, v(8.16, -12.8) * mm, v(7.93, -13.17) * mm, v(7.56, -13.24) * mm, v(7.26, -12.98) * mm, v(7.48, -12.44) * mm, v(7.55, -12.24) * mm, v(7.06, -11.99) * mm, v(6.73, -12.06) * mm, v(6.45, -12.45) * mm, v(6.18, -12.5) * mm, v(5.77, -12.22) * mm, v(5.94, -11.72) * mm, v(5.97, -11.44) * mm, v(5.3, -11.13) * mm, v(4.94, -11.3) * mm, v(4.57, -11.73) * mm, v(4.26, -11.73) * mm, v(4, -11.53) * mm, v(4.14, -11.12) * mm], "startDerivative": vector(5.38, 6.53) * mm, "endDerivative": vector(5.7, 9.27) * mm});
            skPoint(sketch, "E61", {"position": v(8.77, -13.38) * mm});
            skLineSegment(sketch, "E62", {"start": v(8.75, -13.4) * mm, "end": v(8.77, -13.38) * mm});
            skFitSpline(sketch, "E63", {"points": [v(-17.53, -3.22) * mm, v(-16.1, -3.86) * mm, v(-13.11, -3.66) * mm, v(-11.12, -2.6) * mm, v(-9.18, -1.43) * mm, v(-7.88, 0.6) * mm, v(-7.4, 1.57) * mm, v(-7.24, 1.68) * mm, v(-7.12, 1.48) * mm, v(-6.99, 0.85) * mm, v(-7.15, -0.23) * mm, v(-7.73, -1.29) * mm, v(-7.93, -1.65) * mm, v(-8.53, -2.37) * mm, v(-9.42, -3.01) * mm, v(-10.17, -3.48) * mm, v(-10.3, -3.65) * mm, v(-10.23, -4.05) * mm, v(-9.73, -4.64) * mm, v(-9.17, -5.02) * mm, v(-8.5, -5.11) * mm, v(-7.35, -4.59) * mm, v(-6.17, -3.84) * mm, v(-5.08, -2.68) * mm, v(-4.85, -2.06) * mm, v(-4.85, -1.48) * mm, v(-5.1, -1.08) * mm, v(-5.97, -0.89) * mm, v(-6.12, -0.68) * mm, v(-6.02, -0.53) * mm, v(-5.3, -0.4) * mm, v(-4.53, -0.52) * mm, v(-3.96, -0.96) * mm, v(-3.73, -1.73) * mm, v(-3.92, -2.93) * mm, v(-4.48, -3.9) * mm, v(-5.51, -4.97) * mm, v(-6.05, -5.36) * mm, v(-7.39, -6.13) * mm, v(-7.8, -6.33) * mm, v(-7.87, -6.77) * mm, v(-7.33, -7.5) * mm, v(-6.77, -8.04) * mm, v(-6.09, -8.11) * mm, v(-4.06, -7.33) * mm, v(-2.42, -6.17) * mm, v(-1.8, -5.26) * mm, v(-1.54, -4.53) * mm, v(-1.54, -3.84) * mm, v(-1.97, -3.29) * mm, v(-2.5, -2.95) * mm, v(-2.58, -2.78) * mm, v(-2.3, -2.6) * mm, v(-1.9, -2.65) * mm, v(-1.35, -2.87) * mm, v(-0.83, -3.42) * mm, v(-0.5, -4.16) * mm, v(-0.52, -5.34) * mm, v(-1.05, -6.45) * mm, v(-2.3, -7.8) * mm, v(-4.62, -9.06) * mm, v(-5.17, -9.23) * mm, v(-5.33, -9.54) * mm, v(-5.04, -10.09) * mm, v(-4.15, -10.75) * mm, v(-2.89, -10.76) * mm, v(-1.13, -10.19) * mm, v(0.4, -9.08) * mm, v(0.91, -8.23) * mm, v(1.05, -7.79) * mm, v(1.01, -7.15) * mm, v(1, -6.48) * mm, v(1.05, -6.18) * mm, v(1.27, -6.08) * mm, v(1.54, -6.23) * mm, v(1.87, -6.8) * mm, v(2.06, -7.51) * mm, v(1.95, -8.56) * mm, v(1.23, -9.86) * mm, v(0.15, -10.82) * mm, v(-0.83, -11.32) * mm, v(-1.63, -11.55) * mm, v(-2.07, -11.97) * mm, v(-2.07, -12.37) * mm, v(-1.8, -13.04) * mm, v(-1.85, -13.74) * mm, v(-2.27, -14.23) * mm, v(-3.07, -14.25) * mm, v(-3.56, -13.9) * mm, v(-4.07, -13.7) * mm, v(-4.62, -13.7) * mm, v(-5.23, -14.39) * mm, v(-6.8, -15.47) * mm, v(-9.25, -15.96) * mm, v(-10.44, -15.75) * mm, v(-11.35, -15.16) * mm, v(-11.3, -14.9) * mm, v(-10.62, -15) * mm, v(-9.78, -15.16) * mm, v(-8.45, -15.02) * mm, v(-7.28, -14.57) * mm, v(-6.15, -13.73) * mm, v(-5.42, -12.61) * mm, v(-5.38, -11.9) * mm, v(-6.1, -11.01) * mm], "startDerivative": vector(95.22, -61.17) * mm, "endDerivative": vector(-82.52, 82.13) * mm});
            skFitSpline(sketch, "E64", {"points": [v(-6.1, -11.01) * mm, v(-6.3, -10.74) * mm, v(-6.72, -10.7) * mm, v(-7.25, -11.14) * mm, v(-8.37, -12.14) * mm, v(-10.43, -13.16) * mm, v(-11.52, -13.42) * mm, v(-12.51, -13.42) * mm, v(-13.47, -13.15) * mm, v(-14.5, -12.57) * mm, v(-14.87, -12.07) * mm, v(-14.85, -11.54) * mm, v(-14.55, -11.31) * mm], "startDerivative": vector(-3.1, 5.9) * mm, "endDerivative": vector(6.48, 3.12) * mm});
            skFitSpline(sketch, "E65", {"points": [v(-14.85, -11.54) * mm, v(-14.62, -11.2) * mm, v(-14.5, -11.14) * mm, v(-14.4, -11.28) * mm, v(-14.17, -11.6) * mm, v(-13.65, -12) * mm, v(-13.06, -12.19) * mm, v(-11.48, -12.12) * mm, v(-9.68, -11.37) * mm, v(-8.77, -10.63) * mm, v(-8.35, -10.09) * mm, v(-8.36, -9.46) * mm, v(-8.55, -8.98) * mm, v(-9.2, -8.22) * mm, v(-9.43, -8.01) * mm, v(-9.69, -7.68) * mm, v(-9.93, -7.48) * mm, v(-10.06, -7.46) * mm, v(-10.31, -7.74) * mm, v(-11.47, -8.67) * mm, v(-12.84, -9.26) * mm, v(-14.05, -9.4) * mm, v(-15.15, -9.32) * mm, v(-16.19, -8.86) * mm, v(-16.88, -8.47) * mm, v(-17.48, -7.88) * mm, v(-17.8, -7.45) * mm, v(-17.9, -7) * mm, v(-17.93, -6.56) * mm, v(-17.66, -6.14) * mm, v(-17.2, -5.88) * mm, v(-16.95, -5.93) * mm, v(-16.95, -6.23) * mm, v(-16.98, -6.74) * mm, v(-16.66, -7.33) * mm, v(-15.83, -7.79) * mm, v(-14.54, -7.98) * mm, v(-13.2, -7.88) * mm, v(-12.24, -7.5) * mm, v(-11.2, -6.84) * mm, v(-10.91, -6.45) * mm, v(-10.81, -6.04) * mm, v(-10.83, -5.59) * mm, v(-11.16, -5.14) * mm, v(-11.7, -4.66) * mm, v(-12.01, -4.47) * mm, v(-12.58, -4.58) * mm, v(-13.46, -4.8) * mm, v(-14.58, -4.9) * mm, v(-15.86, -4.78) * mm, v(-16.8, -4.55) * mm, v(-17.64, -4.1) * mm, v(-18.11, -3.68) * mm, v(-18.3, -3.37) * mm, v(-18.24, -3.07) * mm, v(-17.79, -3.13) * mm, v(-17.53, -3.22) * mm], "startDerivative": vector(16.77, 27.27) * mm, "endDerivative": vector(19.18, -6.95) * mm});
            skSolve(sketch);
        }
        {
            var Q0;
            Q0=makeQuery(id+"F1.opExtrude","SWEPT_FACE",FACE,{"disambiguationData":[OSD([sQuery(id+"F0.wireOp",EDGE,"E3")])]});
            var sketch = newSketch(context, id + "F4", { "sketchPlane" : qUnion([Q0])});
            skLineSegment(sketch, "E66", {"start": v(1.42, 40.07) * mm, "end": v(5.52, 40.07) * mm});
            skLineSegment(sketch, "E67", {"start": v(5.86, 39.73) * mm, "end": v(5.86, 26.44) * mm});
            skLineSegment(sketch, "E68", {"start": v(5.52, 26.1) * mm, "end": v(1.42, 26.1) * mm});
            skLineSegment(sketch, "E69", {"start": v(1.08, 26.44) * mm, "end": v(1.08, 39.73) * mm});
            skPoint(sketch, "E70.visualSharp", {"position": v(1.08, 40.07) * mm});
            skArc(sketch, "E70.filletArc", {"start": v(1.42, 40.07) * mm, "mid": v(1.17, 39.97) * mm, "end": v(1.08, 39.73) * mm});
            skPoint(sketch, "E71.visualSharp", {"position": v(5.86, 40.07) * mm});
            skArc(sketch, "E71.filletArc", {"start": v(5.86, 39.73) * mm, "mid": v(5.76, 39.97) * mm, "end": v(5.52, 40.07) * mm});
            skPoint(sketch, "E72.visualSharp", {"position": v(5.86, 26.1) * mm});
            skArc(sketch, "E72.filletArc", {"start": v(5.52, 26.1) * mm, "mid": v(5.76, 26.2) * mm, "end": v(5.86, 26.44) * mm});
            skPoint(sketch, "E73.visualSharp", {"position": v(1.08, 26.1) * mm});
            skArc(sketch, "E73.filletArc", {"start": v(1.08, 26.44) * mm, "mid": v(1.17, 26.2) * mm, "end": v(1.42, 26.1) * mm});
            skSolve(sketch);
        }
        {
            var Q0;
            Q0 = qSketchRegion(id + "F4", true);
            extrude(context, id + "F5", {"entities" : qUnion([Q0]), "operationType" : NewBodyOperationType.ADD, "depth" : .8 * mm});
        }
        {
            var Q0;
            Q0=makeQuery(id+"F1.opExtrude","SWEPT_FACE",FACE,{"disambiguationData":[OSD([sQuery(id+"F0.wireOp",EDGE,"E1")])]});
            var sketch = newSketch(context, id + "F6", { "sketchPlane" : qUnion([Q0])});
            skLineSegment(sketch, "E74.bottom", {"start": v(-4.6, 56.94) * mm, "end": v(-2.27, 56.94) * mm});
            skLineSegment(sketch, "E74.top", {"start": v(-4.6, 50.17) * mm, "end": v(-2.27, 50.17) * mm});
            skLineSegment(sketch, "E74.left", {"start": v(-4.6, 56.94) * mm, "end": v(-4.6, 50.17) * mm});
            skLineSegment(sketch, "E74.right", {"start": v(-2.27, 56.94) * mm, "end": v(-2.27, 50.17) * mm});
            skSolve(sketch);
        }
        {
            var Q0;
            Q0 = qSketchRegion(id + "F6", true);
            extrude(context, id + "F7", {"entities" : qUnion([Q0]), "operationType" : NewBodyOperationType.REMOVE, "oppositeDirection" : true, "depth" : 25 * mm});
        }
        {
            var Q0;
            Q0=makeQuery(id+"F1.opExtrude","SWEPT_FACE",FACE,{"disambiguationData":[OSD([sQuery(id+"F0.wireOp",EDGE,"E1")])]});
            var sketch = newSketch(context, id + "F8", { "sketchPlane" : qUnion([Q0])});
            skLineSegment(sketch, "E75.bottom", {"start": v(-4.3, 44.46) * mm, "end": v(-2.86, 44.46) * mm});
            skLineSegment(sketch, "E75.top", {"start": v(-4.3, 37.46) * mm, "end": v(-2.86, 37.46) * mm});
            skLineSegment(sketch, "E75.left", {"start": v(-4.64, 44.12) * mm, "end": v(-4.64, 37.8) * mm});
            skLineSegment(sketch, "E75.right", {"start": v(-2.52, 44.12) * mm, "end": v(-2.52, 37.8) * mm});
            skLineSegment(sketch, "E76.bottom", {"start": v(-4.3, 36.82) * mm, "end": v(-2.86, 36.82) * mm});
            skLineSegment(sketch, "E76.top", {"start": v(-4.3, 29.82) * mm, "end": v(-2.86, 29.82) * mm});
            skLineSegment(sketch, "E76.left", {"start": v(-4.64, 36.48) * mm, "end": v(-4.64, 30.16) * mm});
            skLineSegment(sketch, "E76.right", {"start": v(-2.52, 36.48) * mm, "end": v(-2.52, 30.16) * mm});
            skLineSegment(sketch, "E77", {"start": v(-4.64, 36.82) * mm, "end": v(-4.64, 37.46) * mm});
            skLineSegment(sketch, "E78", {"start": v(-2.52, 36.82) * mm, "end": v(-2.52, 37.46) * mm});
            skPoint(sketch, "E79.visualSharp", {"position": v(-4.64, 29.82) * mm});
            skArc(sketch, "E79.filletArc", {"start": v(-4.64, 30.16) * mm, "mid": v(-4.54, 29.92) * mm, "end": v(-4.3, 29.82) * mm});
            skPoint(sketch, "E80.visualSharp", {"position": v(-2.52, 29.82) * mm});
            skArc(sketch, "E80.filletArc", {"start": v(-2.86, 29.82) * mm, "mid": v(-2.62, 29.92) * mm, "end": v(-2.52, 30.16) * mm});
            skPoint(sketch, "E81.visualSharp", {"position": v(-2.52, 36.82) * mm});
            skArc(sketch, "E81.filletArc", {"start": v(-2.52, 36.48) * mm, "mid": v(-2.62, 36.72) * mm, "end": v(-2.86, 36.82) * mm});
            skPoint(sketch, "E82.visualSharp", {"position": v(-4.64, 36.82) * mm});
            skArc(sketch, "E82.filletArc", {"start": v(-4.3, 36.82) * mm, "mid": v(-4.54, 36.72) * mm, "end": v(-4.64, 36.48) * mm});
            skPoint(sketch, "E83.visualSharp", {"position": v(-2.52, 37.46) * mm});
            skArc(sketch, "E83.filletArc", {"start": v(-2.86, 37.46) * mm, "mid": v(-2.62, 37.56) * mm, "end": v(-2.52, 37.8) * mm});
            skPoint(sketch, "E84.visualSharp", {"position": v(-4.64, 37.46) * mm});
            skArc(sketch, "E84.filletArc", {"start": v(-4.64, 37.8) * mm, "mid": v(-4.54, 37.56) * mm, "end": v(-4.3, 37.46) * mm});
            skPoint(sketch, "E85.visualSharp", {"position": v(-4.64, 44.46) * mm});
            skArc(sketch, "E85.filletArc", {"start": v(-4.3, 44.46) * mm, "mid": v(-4.54, 44.36) * mm, "end": v(-4.64, 44.12) * mm});
            skPoint(sketch, "E86.visualSharp", {"position": v(-2.52, 44.46) * mm});
            skArc(sketch, "E86.filletArc", {"start": v(-2.52, 44.12) * mm, "mid": v(-2.62, 44.36) * mm, "end": v(-2.86, 44.46) * mm});
            skSolve(sketch);
        }
        {
            var Q0;
            Q0 = qSketchRegion(id + "F8", true);
            extrude(context, id + "F9", {"entities" : qUnion([Q0]), "operationType" : NewBodyOperationType.ADD, "depth" : 0.8 * mm});
        }
        {
            var Q0;
            Q0=makeQuery(id+"F1.opExtrude","SWEPT_FACE",FACE,{"disambiguationData":[OSD([sQuery(id+"F0.wireOp",EDGE,"E2")])]});
            var sketch = newSketch(context, id + "F10", { "sketchPlane" : qUnion([Q0])});
            skLineSegment(sketch, "E87.bottom", {"start": v(-26.61, -1.83) * mm, "end": v(-15.87, -1.83) * mm});
            skLineSegment(sketch, "E87.top", {"start": v(-26.61, -5.77) * mm, "end": v(-15.87, -5.77) * mm});
            skLineSegment(sketch, "E87.left", {"start": v(-26.61, -1.83) * mm, "end": v(-26.61, -5.77) * mm});
            skLineSegment(sketch, "E87.right", {"start": v(-15.87, -1.83) * mm, "end": v(-15.87, -5.77) * mm});
            skLineSegment(sketch, "E88.bottom", {"start": v(25.35, -1.83) * mm, "end": v(10.3, -1.83) * mm});
            skLineSegment(sketch, "E88.top", {"start": v(25.35, -5.13) * mm, "end": v(10.3, -5.13) * mm});
            skLineSegment(sketch, "E88.left", {"start": v(25.35, -1.83) * mm, "end": v(25.35, -5.13) * mm});
            skLineSegment(sketch, "E88.right", {"start": v(10.3, -1.83) * mm, "end": v(10.3, -5.13) * mm});
            skLineSegment(sketch, "E89.bottom", {"start": v(-7.6, -1.83) * mm, "end": v(3, -1.83) * mm});
            skLineSegment(sketch, "E89.top", {"start": v(-7.6, -6.48) * mm, "end": v(3, -6.48) * mm});
            skLineSegment(sketch, "E89.left", {"start": v(-7.6, -1.83) * mm, "end": v(-7.6, -6.48) * mm});
            skLineSegment(sketch, "E89.right", {"start": v(3, -1.83) * mm, "end": v(3, -6.48) * mm});
            skSolve(sketch);
        }
        {
            var Q0;
            Q0 = qSketchRegion(id + "F10", true);
            extrude(context, id + "F11", {"entities" : qUnion([Q0]), "operationType" : NewBodyOperationType.REMOVE, "oppositeDirection" : true, "depth" : 25 * mm});
        }
        {
            var Q0;
            Q0=makeQuery(id+"F3.imprint","IMPRINT",FACE,{"disambiguationData":[TD([[makeQuery(id+"F3.imprint","IMPRINT",EDGE,{"derivedFrom":sQuery(id+"F3.wireOp",EDGE,"E33")}),1.0]])]});
            var Q1;
            Q1=makeQuery(id+"F3.imprint","IMPRINT",FACE,{"disambiguationData":[TD([[makeQuery(id+"F3.imprint","IMPRINT",EDGE,{"derivedFrom":sQuery(id+"F3.wireOp",EDGE,"E27")}),-1.0]])]});
            var Q2;
            Q2=makeQuery(id+"F3.imprint","IMPRINT",FACE,{"disambiguationData":[TD([[makeQuery(id+"F3.imprint","IMPRINT",EDGE,{"derivedFrom":sQuery(id+"F3.wireOp",EDGE,"E35")}),-1.0]])]});
            var Q3;
            Q3=makeQuery(id+"F3.imprint","IMPRINT",FACE,{"disambiguationData":[TD([[makeQuery(id+"F3.imprint","IMPRINT",EDGE,{"derivedFrom":sQuery(id+"F3.wireOp",EDGE,"E8")}),-1.0]])]});
            extrude(context, id + "F12", {"entities" : qUnion([Q0, Q1, Q2, Q3]), "operationType" : NewBodyOperationType.ADD, "depth" : 1 * mm});
        }
    });
